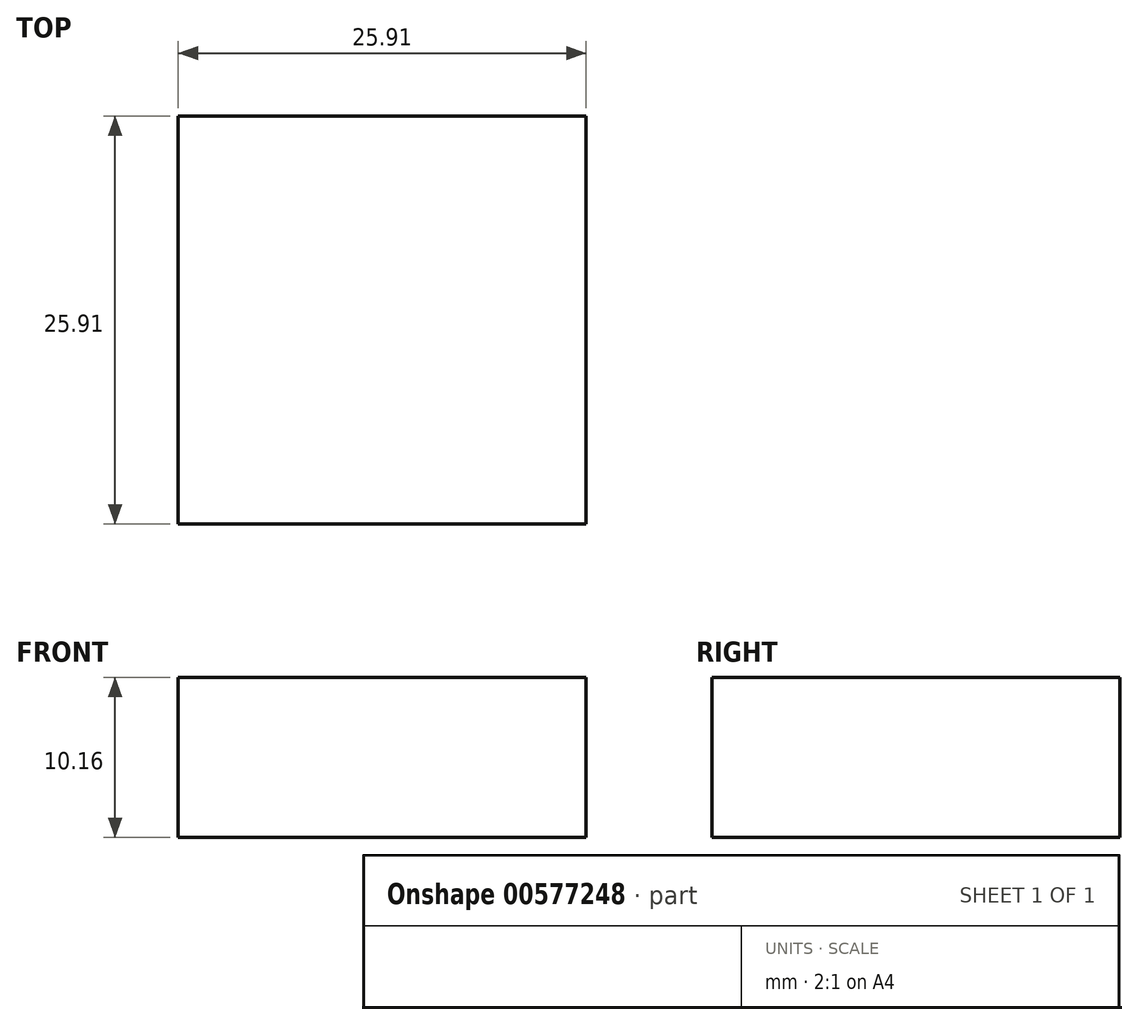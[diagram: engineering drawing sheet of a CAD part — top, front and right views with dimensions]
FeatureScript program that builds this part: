
annotation { "Feature Type Name" : "Feature", "Feature Type Description" : "" }
export const myFeature = defineFeature(function(context is Context, id is Id, definition is map)
    precondition{}
    {
        {
            var Q0;
            Q0=qCreatedBy(makeId("Top.planeOp"),FACE);
            var sketch = newSketch(context, id + "F0", { "sketchPlane" : qUnion([Q0])});
            skLineSegment(sketch, "E0.bottom", {"start": v(-25.9, 9.67) * mm, "end": v(0, 9.67) * mm});
            skLineSegment(sketch, "E0.top", {"start": v(-25.9, -16.24) * mm, "end": v(0, -16.24) * mm});
            skLineSegment(sketch, "E0.left", {"start": v(-25.9, 9.67) * mm, "end": v(-25.9, -16.24) * mm});
            skLineSegment(sketch, "E0.right", {"start": v(0, 9.67) * mm, "end": v(0, -16.24) * mm});
            skSolve(sketch);
        }
        {
            var Q0;
            Q0 = qSketchRegion(id + "F0", true);
            extrude(context, id + "F1", {"entities" : qUnion([Q0]), "depth" : 10.16 * mm, "offsetDistance" : 25.4 * mm});
        }
    });
